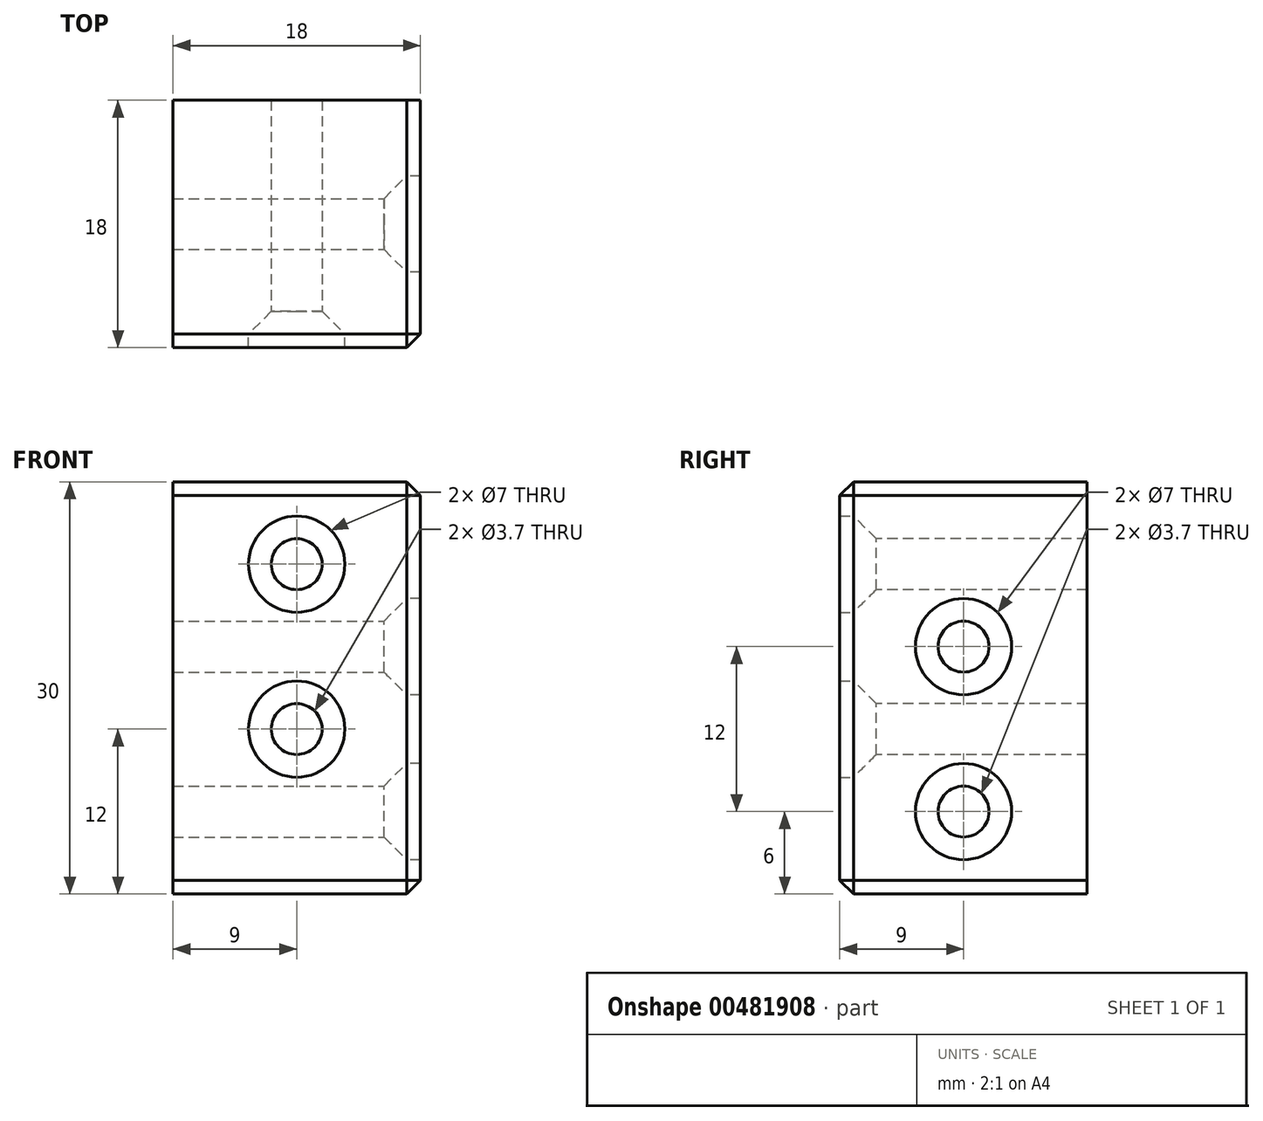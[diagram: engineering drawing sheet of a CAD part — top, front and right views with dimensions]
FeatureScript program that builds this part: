
annotation { "Feature Type Name" : "Feature", "Feature Type Description" : "" }
export const myFeature = defineFeature(function(context is Context, id is Id, definition is map)
    precondition{}
    {
        {
            var Q0;
            Q0=qCreatedBy(makeId("Front.planeOp"),FACE);
            var sketch = newSketch(context, id + "F0", { "sketchPlane" : qUnion([Q0])});
            skLineSegment(sketch, "E0.bottom", {"start": v(-9, 0) * mm, "end": v(9, 0) * mm});
            skLineSegment(sketch, "E0.top", {"start": v(-9, 30) * mm, "end": v(9, 30) * mm});
            skLineSegment(sketch, "E0.left", {"start": v(-9, 0) * mm, "end": v(-9, 30) * mm});
            skLineSegment(sketch, "E0.right", {"start": v(9, 0) * mm, "end": v(9, 30) * mm});
            skSolve(sketch);
        }
        {
            var Q0;
            Q0=makeQuery(id+"F0.imprint","IMPRINT",FACE,{"disambiguationData":[TD([[makeQuery(id+"F0.imprint","IMPRINT",EDGE,{"derivedFrom":sQuery(id+"F0.wireOp",EDGE,"E0.bottom")}),1.0]])]});
            extrude(context, id + "F1", {"entities" : qUnion([Q0]), "depth" : 18 * mm});
        }
        {
            var Q0;
            Q0=makeQuery(id+"F1.opExtrude","CAP_FACE",FACE,{"disambiguationData":[OSD([sQuery(id+"F0.wireOp",EDGE,"E0.bottom"),sQuery(id+"F0.wireOp",EDGE,"E0.top"),sQuery(id+"F0.wireOp",EDGE,"E0.left"),sQuery(id+"F0.wireOp",EDGE,"E0.right")])],"isStart":false});
            cPlane(context, id + "F2", {"entities" : qUnion([Q0]), "cplaneType" : CPlaneType.OFFSET, "offset" : 1 * mm, "oppositeDirection" : true, "width" : 150 * mm, "height" : 150 * mm});
        }
        {
            var Q0;
            Q0=qCreatedBy(id+"F2.planeOp",FACE);
            var sketch = newSketch(context, id + "F3", { "sketchPlane" : qUnion([Q0])});
            skPoint(sketch, "E1", {"position": v(0, 24) * mm});
            skPoint(sketch, "E2", {"position": v(0, 12) * mm});
            skSolve(sketch);
        }
        {
            var Q0;
            Q0=sQuery(id+"F3.wireOp",VERTEX,"E1");
            var Q1;
            Q1=sQuery(id+"F3.wireOp",VERTEX,"E2");
            var Q2;
            Q2=makeQuery(id+"F1.opExtrude","SWEPT_BODY",BODY,{"disambiguationData":[OSD([sQuery(id+"F0.wireOp",EDGE,"E0.bottom"),sQuery(id+"F0.wireOp",EDGE,"E0.top"),sQuery(id+"F0.wireOp",EDGE,"E0.left"),sQuery(id+"F0.wireOp",EDGE,"E0.right")])]});
            hole(context, id + "F4", {"style" : HoleStyle.SIMPLE, "endStyle" : HoleEndStyle.THROUGH, "oppositeDirection" : true, "holeDiameter" : 7 * mm, "isTappedThrough" : true, "tappedDepth" : 12 * mm, "tapClearance" : 3, "locations" : qUnion([Q0, Q1]), "scope" : qUnion([Q2])});
        }
        {
            var Q0;
            Q0=sQuery(id+"F3.wireOp",VERTEX,"E1");
            var Q1;
            Q1=sQuery(id+"F3.wireOp",VERTEX,"E2");
            var Q2;
            Q2=makeQuery(id+"F1.opExtrude","SWEPT_BODY",BODY,{"disambiguationData":[OSD([sQuery(id+"F0.wireOp",EDGE,"E0.bottom"),sQuery(id+"F0.wireOp",EDGE,"E0.top"),sQuery(id+"F0.wireOp",EDGE,"E0.left"),sQuery(id+"F0.wireOp",EDGE,"E0.right")])]});
            hole(context, id + "F5", {"style" : HoleStyle.C_SINK, "endStyle" : HoleEndStyle.THROUGH, "holeDiameter" : 3.7 * mm, "cSinkDiameter" : 7 * mm, "cSinkAngle" : 90 * degree, "isTappedThrough" : true, "tappedDepth" : 12 * mm, "tapClearance" : 3, "locations" : qUnion([Q0, Q1]), "scope" : qUnion([Q2])});
        }
        {
            var Q0;
            Q0=makeQuery(id+"F1.opExtrude","SWEPT_FACE",FACE,{"disambiguationData":[OSD([sQuery(id+"F0.wireOp",EDGE,"E0.right")])]});
            cPlane(context, id + "F6", {"entities" : qUnion([Q0]), "cplaneType" : CPlaneType.OFFSET, "offset" : 1 * mm, "oppositeDirection" : true, "width" : 150 * mm, "height" : 150 * mm});
        }
        {
            var Q0;
            Q0=qCreatedBy(id+"F6.planeOp",FACE);
            var sketch = newSketch(context, id + "F7", { "sketchPlane" : qUnion([Q0])});
            skPoint(sketch, "E3", {"position": v(-9, 18) * mm});
            skPoint(sketch, "E4", {"position": v(-9, 6) * mm});
            skPoint(sketch, "E5", {"position": v(-9, 0) * mm});
            skSolve(sketch);
        }
        {
            var Q0;
            Q0=sQuery(id+"F7.wireOp",VERTEX,"E3");
            var Q1;
            Q1=sQuery(id+"F7.wireOp",VERTEX,"E4");
            var Q2;
            Q2=makeQuery(id+"F1.opExtrude","SWEPT_BODY",BODY,{"disambiguationData":[OSD([sQuery(id+"F0.wireOp",EDGE,"E0.bottom"),sQuery(id+"F0.wireOp",EDGE,"E0.top"),sQuery(id+"F0.wireOp",EDGE,"E0.left"),sQuery(id+"F0.wireOp",EDGE,"E0.right")])]});
            hole(context, id + "F8", {"style" : HoleStyle.SIMPLE, "endStyle" : HoleEndStyle.THROUGH, "oppositeDirection" : true, "holeDiameter" : 7 * mm, "isTappedThrough" : true, "tappedDepth" : 12 * mm, "tapClearance" : 3, "locations" : qUnion([Q0, Q1]), "scope" : qUnion([Q2])});
        }
        {
            var Q0;
            Q0=sQuery(id+"F7.wireOp",VERTEX,"E3");
            var Q1;
            Q1=sQuery(id+"F7.wireOp",VERTEX,"E4");
            var Q2;
            Q2=makeQuery(id+"F1.opExtrude","SWEPT_BODY",BODY,{"disambiguationData":[OSD([sQuery(id+"F0.wireOp",EDGE,"E0.bottom"),sQuery(id+"F0.wireOp",EDGE,"E0.top"),sQuery(id+"F0.wireOp",EDGE,"E0.left"),sQuery(id+"F0.wireOp",EDGE,"E0.right")])]});
            hole(context, id + "F9", {"style" : HoleStyle.C_SINK, "endStyle" : HoleEndStyle.THROUGH, "holeDiameter" : 3.7 * mm, "cSinkDiameter" : 7 * mm, "cSinkAngle" : 90 * degree, "isTappedThrough" : true, "tappedDepth" : 12 * mm, "tapClearance" : 3, "locations" : qUnion([Q0, Q1]), "scope" : qUnion([Q2])});
        }
        {
            var Q0;
            Q0=makeQuery(id+"F1.opExtrude","CAP_EDGE",EDGE,{"disambiguationData":[OSD([sQuery(id+"F0.wireOp",EDGE,"E0.right")])],"isStart":false});
            var Q1;
            Q1=makeQuery(id+"F1.opExtrude","SWEPT_EDGE",EDGE,{"disambiguationData":[OSD([sQuery(id+"F0.wireOp",EDGE,"E0.top"),sQuery(id+"F0.wireOp",EDGE,"E0.right")])]});
            var Q2;
            Q2=makeQuery(id+"F1.opExtrude","CAP_EDGE",EDGE,{"disambiguationData":[OSD([sQuery(id+"F0.wireOp",EDGE,"E0.top")])],"isStart":false});
            var Q3;
            Q3=makeQuery(id+"F1.opExtrude","SWEPT_EDGE",EDGE,{"disambiguationData":[OSD([sQuery(id+"F0.wireOp",EDGE,"E0.bottom"),sQuery(id+"F0.wireOp",EDGE,"E0.right")])]});
            var Q4;
            Q4=makeQuery(id+"F1.opExtrude","CAP_EDGE",EDGE,{"disambiguationData":[OSD([sQuery(id+"F0.wireOp",EDGE,"E0.bottom")])],"isStart":false});
            chamfer(context, id + "F10", {"entities" : qUnion([Q0, Q1, Q2, Q3, Q4]), "width" : 1 * mm, "tangentPropagation" : true});
        }
    });
